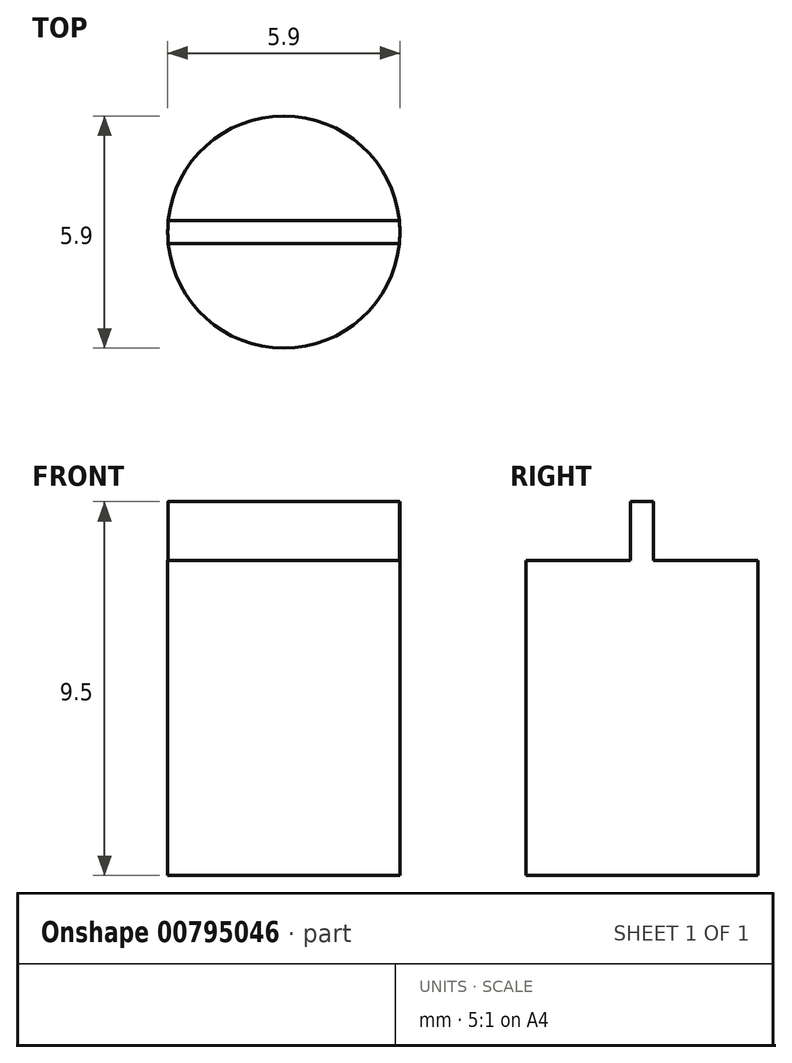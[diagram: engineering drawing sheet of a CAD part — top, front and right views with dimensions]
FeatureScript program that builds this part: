
annotation { "Feature Type Name" : "Feature", "Feature Type Description" : "" }
export const myFeature = defineFeature(function(context is Context, id is Id, definition is map)
    precondition{}
    {
        {
            var Q0;
            Q0=qCreatedBy(makeId("Top.planeOp"),FACE);
            var sketch = newSketch(context, id + "F0", { "sketchPlane" : qUnion([Q0])});
            skCircle(sketch, "E0", {"center": v(0, 0) * mm, "radius": 2.95 * mm});
            skSolve(sketch);
        }
        {
            var Q0;
            Q0=makeQuery(id+"F0.imprint","IMPRINT",FACE,{"disambiguationData":[TD([[makeQuery(id+"F0.imprint","IMPRINT",EDGE,{"derivedFrom":sQuery(id+"F0.wireOp",EDGE,"E0")}),1.0]])]});
            extrude(context, id + "F1", {"entities" : qUnion([Q0]), "depth" : 8 * mm, "offsetDistance" : 25.4 * mm});
        }
        {
            var Q0;
            Q0=makeQuery(id+"F1.opExtrude","CAP_FACE",FACE,{"disambiguationData":[OSD([sQuery(id+"F0.wireOp",EDGE,"E0")])],"isStart":false});
            var sketch = newSketch(context, id + "F2", { "sketchPlane" : qUnion([Q0])});
            skLineSegment(sketch, "E1", {"start": v(-2.94, 0.3) * mm, "end": v(2.94, 0.3) * mm});
            skLineSegment(sketch, "E2.MirrorCS", {"start": v(-2.94, -0.3) * mm, "end": v(2.94, -0.3) * mm});
            skArc(sketch, "E3", {"start": v(-2.94, 0.3) * mm, "mid": v(-2.95, 0) * mm, "end": v(-2.94, -0.3) * mm});
            skArc(sketch, "E4", {"start": v(2.94, -0.3) * mm, "mid": v(2.95, 0) * mm, "end": v(2.94, 0.3) * mm});
            skSolve(sketch);
        }
        {
            var Q0;
            {var subQ0=sQuery(id+"F2.wireOp",EDGE,"E1");Q0=makeQuery(id+"F2.imprint","IMPRINT",FACE,{"disambiguationData":[TD([[makeQuery(id+"F2.imprint","IMPRINT",EDGE,{"derivedFrom":subQ0}),-1.0]])]});}
            extrude(context, id + "F3", {"entities" : qUnion([Q0]), "operationType" : NewBodyOperationType.ADD, "depth" : 1.5 * mm, "offsetDistance" : 25.4 * mm});
        }
    });
